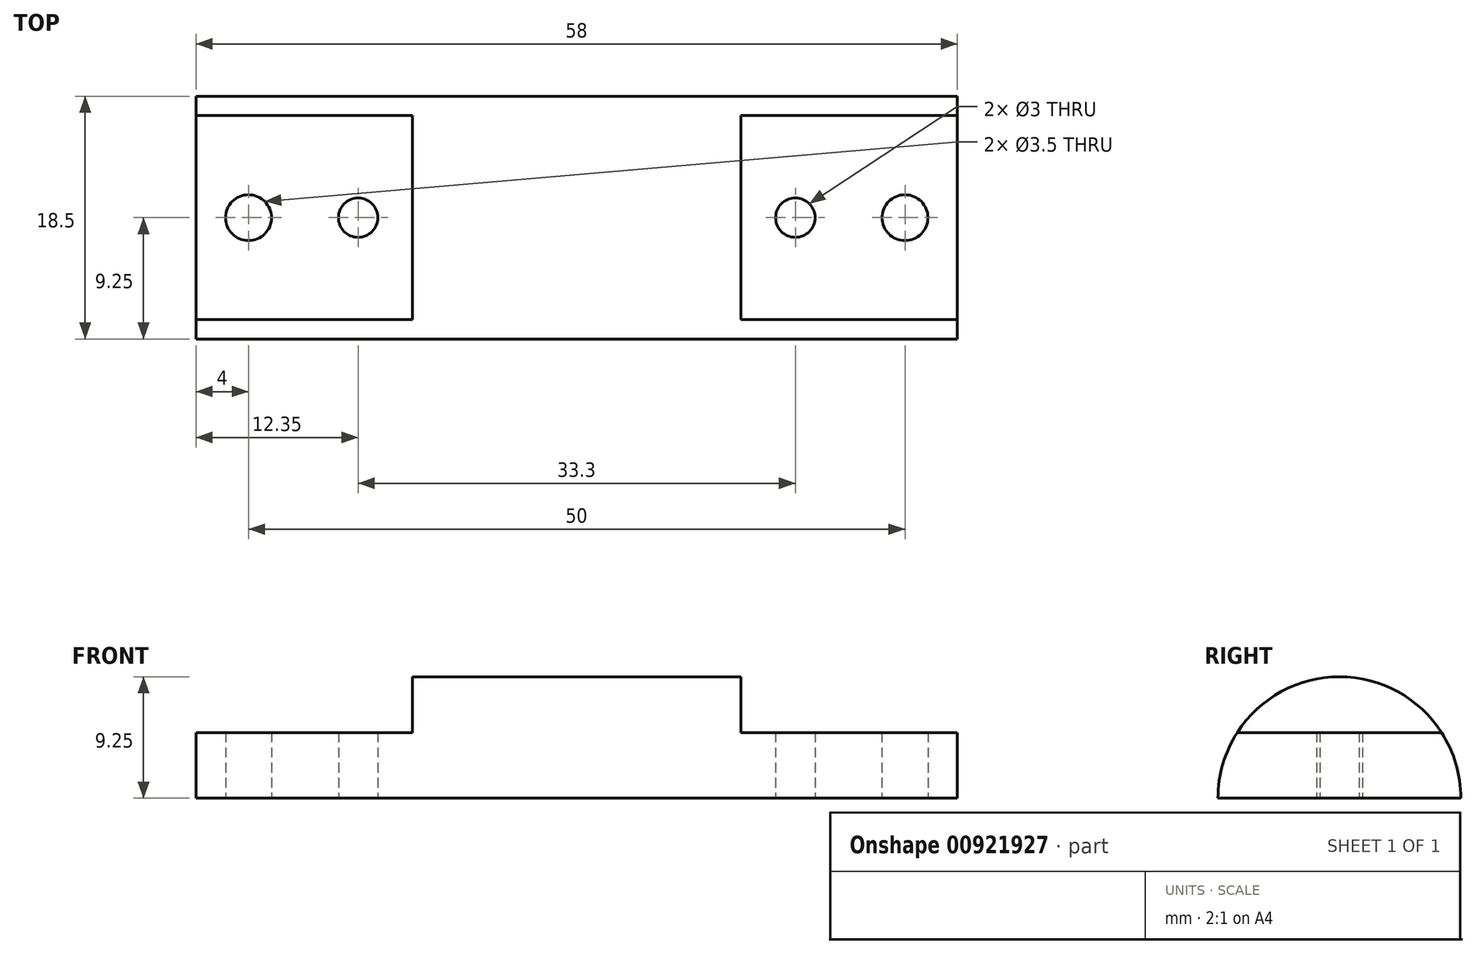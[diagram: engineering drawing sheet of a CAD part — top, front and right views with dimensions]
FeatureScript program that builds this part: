
annotation { "Feature Type Name" : "Feature", "Feature Type Description" : "" }
export const myFeature = defineFeature(function(context is Context, id is Id, definition is map)
    precondition{}
    {
        {
            var Q0;
            Q0=qCreatedBy(makeId("Top.planeOp"),FACE);
            var sketch = newSketch(context, id + "F0", { "sketchPlane" : qUnion([Q0])});
            skLineSegment(sketch, "E0.bottom", {"start": v(19, -9.25) * mm, "end": v(-19, -9.25) * mm});
            skLineSegment(sketch, "E0.top", {"start": v(19, 9.25) * mm, "end": v(-19, 9.25) * mm});
            skLineSegment(sketch, "E0.left", {"start": v(19, -9.25) * mm, "end": v(19, 9.25) * mm});
            skLineSegment(sketch, "E0.right", {"start": v(-19, -9.25) * mm, "end": v(-19, 9.25) * mm});
            skPoint(sketch, "E0.middle", {"position": v(0, 0) * mm});
            skLineSegment(sketch, "E1.bottom", {"start": v(19, -9.25) * mm, "end": v(29, -9.25) * mm});
            skLineSegment(sketch, "E1.top", {"start": v(19, 9.25) * mm, "end": v(29, 9.25) * mm});
            skLineSegment(sketch, "E1.right", {"start": v(29, -9.25) * mm, "end": v(29, 9.25) * mm});
            skLineSegment(sketch, "E2.bottom", {"start": v(-19, -9.25) * mm, "end": v(-29, -9.25) * mm});
            skLineSegment(sketch, "E2.top", {"start": v(-19, 9.25) * mm, "end": v(-29, 9.25) * mm});
            skLineSegment(sketch, "E2.right", {"start": v(-29, -9.25) * mm, "end": v(-29, 9.25) * mm});
            skCircle(sketch, "E3", {"center": v(-25, 0) * mm, "radius": 1.75 * mm});
            skPoint(sketch, "E3.centerSnap0", {"position": v(-29, 0) * mm});
            skCircle(sketch, "E4", {"center": v(25, 0) * mm, "radius": 1.75 * mm});
            skPoint(sketch, "E4.centerSnap0", {"position": v(29, 0) * mm});
            skCircle(sketch, "E5", {"center": v(-16.65, 0) * mm, "radius": 1.5 * mm});
            skCircle(sketch, "E6", {"center": v(16.65, 0) * mm, "radius": 1.5 * mm});
            skSolve(sketch);
        }
        {
            var Q0;
            Q0=qSketchRegion(id+"F0",true);
            extrude(context, id + "F1", {"entities" : qUnion([Q0]), "depth" : 5 * mm, "offsetDistance" : 25 * mm});
        }
        {
            var Q0;
            Q0=makeQuery(id+"F1.opExtrude","CAP_FACE",FACE,{"disambiguationData":[OSD([sQuery(id+"F0.wireOp",EDGE,"E0.bottom"),sQuery(id+"F0.wireOp",EDGE,"E0.top"),sQuery(id+"F0.wireOp",EDGE,"E1.bottom"),sQuery(id+"F0.wireOp",EDGE,"E1.top"),sQuery(id+"F0.wireOp",EDGE,"E1.right"),sQuery(id+"F0.wireOp",EDGE,"E2.bottom"),sQuery(id+"F0.wireOp",EDGE,"E2.top"),sQuery(id+"F0.wireOp",EDGE,"E2.right"),sQuery(id+"F0.wireOp",EDGE,"E3"),sQuery(id+"F0.wireOp",EDGE,"E4"),sQuery(id+"F0.wireOp",EDGE,"E5"),sQuery(id+"F0.wireOp",EDGE,"E6")])],"isStart":false});
            var sketch = newSketch(context, id + "F2", { "sketchPlane" : qUnion([Q0])});
            skLineSegment(sketch, "E7.bottom", {"start": v(12.5, -9.25) * mm, "end": v(-12.5, -9.25) * mm});
            skLineSegment(sketch, "E7.top", {"start": v(12.5, 9.25) * mm, "end": v(-12.5, 9.25) * mm});
            skLineSegment(sketch, "E7.left", {"start": v(12.5, -9.25) * mm, "end": v(12.5, 9.25) * mm});
            skLineSegment(sketch, "E7.right", {"start": v(-12.5, -9.25) * mm, "end": v(-12.5, 9.25) * mm});
            skPoint(sketch, "E7.middle", {"position": v(0, 0) * mm});
            skSolve(sketch);
        }
        {
            var Q0;
            Q0=qSketchRegion(id+"F2",true);
            extrude(context, id + "F3", {"entities" : qUnion([Q0]), "operationType" : NewBodyOperationType.ADD, "depth" : 18.5 / 2 * mm, "offsetDistance" : 25 * mm});
        }
        {
            var Q0;
            Q0=makeQuery(id+"F1.opExtrude","SWEPT_FACE",FACE,{"disambiguationData":[OSD([sQuery(id+"F0.wireOp",EDGE,"E2.right")])]});
            var sketch = newSketch(context, id + "F4", { "sketchPlane" : qUnion([Q0])});
            skArc(sketch, "E8", {"start": v(9.25, 0) * mm, "mid": v(0, 9.25) * mm, "end": v(-9.25, 0) * mm});
            skLineSegment(sketch, "E9", {"start": v(-9.25, 0) * mm, "end": v(9.25, 0) * mm});
            skLineSegment(sketch, "E10.bottom", {"start": v(-9.25, 0) * mm, "end": v(9.75, 0) * mm});
            skLineSegment(sketch, "E10.top", {"start": v(-9.25, 19) * mm, "end": v(9.75, 19) * mm});
            skLineSegment(sketch, "E10.left", {"start": v(-9.25, 0) * mm, "end": v(-9.25, 19) * mm});
            skLineSegment(sketch, "E10.right", {"start": v(9.75, 0) * mm, "end": v(9.75, 19) * mm});
            skSolve(sketch);
        }
        {
            var Q0;
            {var subQ1=sQuery(id+"F0.wireOp",EDGE,"E2.right");var subQ2=makeQuery(id+"F1.opExtrude","SWEPT_EDGE",EDGE,{"disambiguationData":[OSD([sQuery(id+"F0.wireOp",EDGE,"E2.bottom"),subQ1])]});Q0=makeQuery(id+"F4.imprint","IMPRINT",FACE,{"disambiguationData":[TD([[makeQuery(id+"F4.imprint","IMPRINT",EDGE,{"derivedFrom":subQ2}),-1.0]])]});}
            var Q1;
            {var subQ0=sQuery(id+"F4.wireOp",EDGE,"E10.left");var subQ3=makeQuery(id+"F1.opExtrude","CAP_EDGE",EDGE,{"disambiguationData":[OSD([sQuery(id+"F0.wireOp",EDGE,"E2.right")])],"isStart":false});var subQ5=makeQuery(id+"F4.imprint","INTERSECT",VERTEX,{"derivedFrom":[subQ3,subQ0]});Q1=makeQuery(id+"F4.imprint","IMPRINT",FACE,{"disambiguationData":[TD([[makeQuery(id+"F4.imprint","IMPRINT",EDGE,{"disambiguationData":[TD([[subQ5,1.0]])],"derivedFrom":subQ3}),1.0]])]});}
            var Q2;
            {var subQ0=sQuery(id+"F4.wireOp",EDGE,"E10.top");Q2=makeQuery(id+"F4.imprint","IMPRINT",FACE,{"disambiguationData":[TD([[makeQuery(id+"F4.imprint","IMPRINT",EDGE,{"derivedFrom":subQ0}),-1.0]])]});}
            extrude(context, id + "F5", {"entities" : qUnion([Q0, Q1, Q2]), "operationType" : NewBodyOperationType.REMOVE, "endBound" : BoundingType.THROUGH_ALL, "oppositeDirection" : true, "depth" : 25 * mm, "offsetDistance" : 25 * mm});
        }
    });
